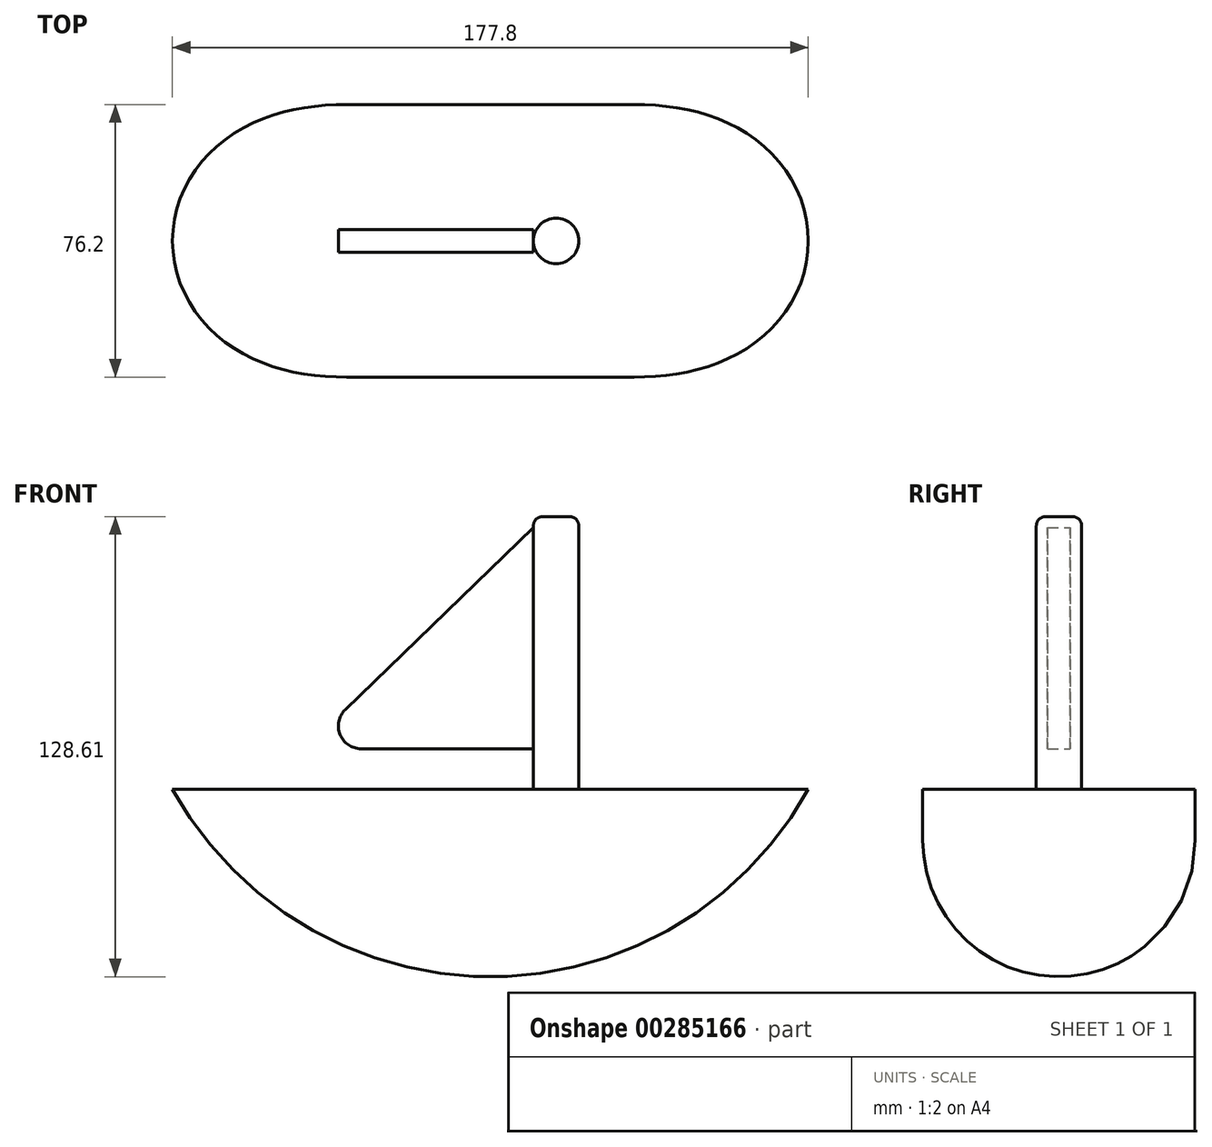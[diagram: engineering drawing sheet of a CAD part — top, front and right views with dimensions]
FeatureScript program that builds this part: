
annotation { "Feature Type Name" : "Feature", "Feature Type Description" : "" }
export const myFeature = defineFeature(function(context is Context, id is Id, definition is map)
    precondition{}
    {
        {
            var Q0;
            Q0=qCreatedBy(makeId("Front.planeOp"),FACE);
            var sketch = newSketch(context, id + "F0", { "sketchPlane" : qUnion([Q0])});
            skLineSegment(sketch, "E0", {"start": v(-88.9, 0) * mm, "end": v(88.9, 0) * mm});
            skArc(sketch, "E1", {"start": v(-88.9, 0) * mm, "mid": v(0, -52.41) * mm, "end": v(88.9, 0) * mm});
            skSolve(sketch);
        }
        {
            var Q0;
            Q0=qCreatedBy(makeId("Front.planeOp"),FACE);
            var sketch = newSketch(context, id + "F1", { "sketchPlane" : qUnion([Q0])});
            skLineSegment(sketch, "E2", {"start": v(24.72, 0) * mm, "end": v(24.72, 76.2) * mm});
            skLineSegment(sketch, "E3", {"start": v(24.72, 76.2) * mm, "end": v(12.02, 76.2) * mm});
            skLineSegment(sketch, "E4", {"start": v(12.02, 0) * mm, "end": v(12.02, 76.2) * mm});
            skLineSegment(sketch, "E5", {"start": v(12.02, 76.2) * mm, "end": v(12.02, 0) * mm});
            skLineSegment(sketch, "E6", {"start": v(12.02, 0) * mm, "end": v(24.72, 0) * mm});
            skLineSegment(sketch, "E7", {"start": v(18.37, 76.2) * mm, "end": v(18.37, 0) * mm});
            skLineSegment(sketch, "E8", {"start": v(12.02, 73.15) * mm, "end": v(-40.6, 22.25) * mm});
            skLineSegment(sketch, "E9", {"start": v(-36.18, 11.33) * mm, "end": v(12.02, 11.33) * mm});
            skPoint(sketch, "E10.visualSharp", {"position": v(-51.87, 11.33) * mm});
            skArc(sketch, "E10.filletArc", {"start": v(-40.6, 22.25) * mm, "mid": v(-42.06, 15.3) * mm, "end": v(-36.18, 11.33) * mm});
            skSolve(sketch);
        }
        {
            var Q0;
            Q0=makeQuery(id+"F0.imprint","IMPRINT",FACE,{"disambiguationData":[TD([[makeQuery(id+"F0.imprint","IMPRINT",EDGE,{"derivedFrom":sQuery(id+"F0.wireOp",EDGE,"E0")}),-1.0]])]});
            extrude(context, id + "F2", {"entities" : qUnion([Q0]), "endBound" : BoundingType.SYMMETRIC, "depth" : 76.2 * mm});
        }
        {
            var Q0;
            {var subQ0=sQuery(id+"F1.wireOp",EDGE,"E2");Q0=makeQuery(id+"F1.imprint","IMPRINT",FACE,{"disambiguationData":[TD([[makeQuery(id+"F1.imprint","IMPRINT",EDGE,{"derivedFrom":subQ0}),1.0]])]});}
            var Q1;
            Q1=sQuery(id+"F1.wireOp",EDGE,"E7");
            revolve(context, id + "F3", {"entities" : qUnion([Q0]), "axis" : qUnion([Q1]), "revolveType" : RevolveType.FULL});
        }
        {
            var Q0;
            {var subQ0=sQuery(id+"F1.wireOp",EDGE,"E8");Q0=makeQuery(id+"F1.imprint","IMPRINT",FACE,{"disambiguationData":[TD([[makeQuery(id+"F1.imprint","IMPRINT",EDGE,{"derivedFrom":subQ0}),1.0]])]});}
            extrude(context, id + "F4", {"entities" : qUnion([Q0]), "operationType" : NewBodyOperationType.ADD, "endBound" : BoundingType.SYMMETRIC, "depth" : 6.35 * mm});
        }
        {
            var Q0;
            Q0=makeQuery(id+"F2.opExtrude","CAP_EDGE",EDGE,{"disambiguationData":[OSD([sQuery(id+"F0.wireOp",EDGE,"E1")])],"isStart":false});
            var Q1;
            Q1=makeQuery(id+"F2.opExtrude","CAP_EDGE",EDGE,{"disambiguationData":[OSD([sQuery(id+"F0.wireOp",EDGE,"E1")])],"isStart":true});
            fillet(context, id + "F5", {"entities" : qUnion([Q0, Q1]), "radius" : 38.1 * mm, "tangentPropagation" : true, "allowEdgeOverflow" : false});
        }
        {
            var Q0;
            Q0=makeQuery(id+"F3.opRevolve","SWEPT_EDGE",EDGE,{"disambiguationData":[OSD([sQuery(id+"F1.wireOp",EDGE,"E2"),sQuery(id+"F1.wireOp",EDGE,"E3")])]});
            fillet(context, id + "F6", {"entities" : qUnion([Q0]), "radius" : 2.54 * mm, "tangentPropagation" : true, "allowEdgeOverflow" : false});
        }
    });
